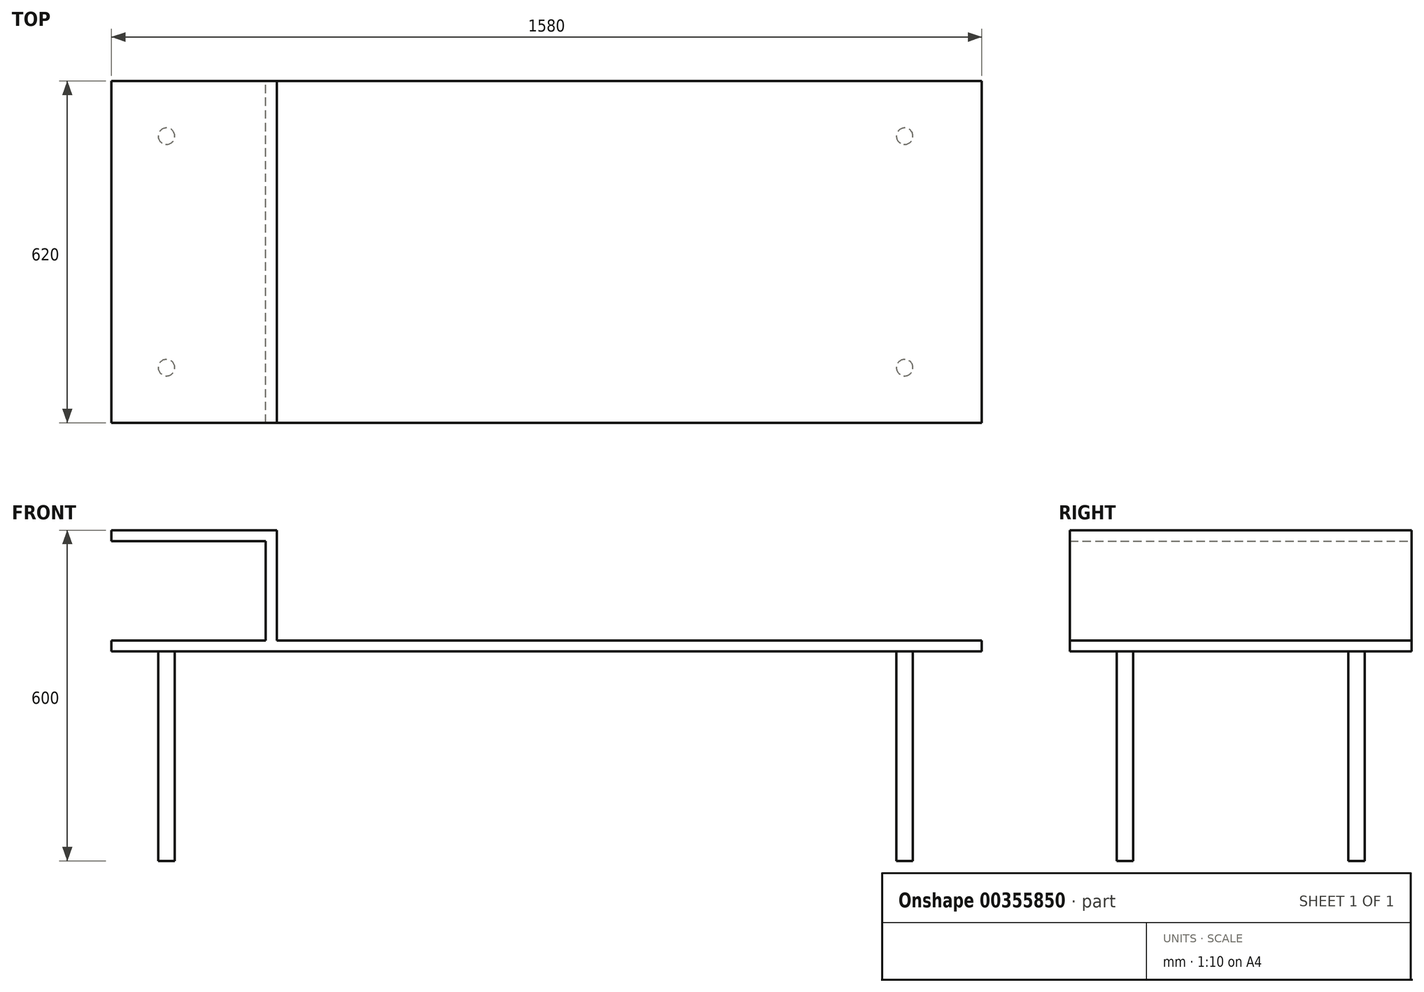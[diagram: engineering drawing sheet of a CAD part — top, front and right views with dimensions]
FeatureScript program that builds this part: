
annotation { "Feature Type Name" : "Feature", "Feature Type Description" : "" }
export const myFeature = defineFeature(function(context is Context, id is Id, definition is map)
    precondition{}
    {
        {
            var Q0;
            Q0=qCreatedBy(makeId("Front.planeOp"),FACE);
            var sketch = newSketch(context, id + "F0", { "sketchPlane" : qUnion([Q0])});
            skLineSegment(sketch, "E0.bottom", {"start": v(-20.5, 31.87) * mm, "end": v(1259.5, 31.87) * mm});
            skLineSegment(sketch, "E0.top", {"start": v(-20.5, 11.87) * mm, "end": v(1259.5, 11.87) * mm});
            skLineSegment(sketch, "E0.left", {"start": v(-20.5, 31.87) * mm, "end": v(-20.5, 11.87) * mm});
            skLineSegment(sketch, "E0.right", {"start": v(1259.5, 31.87) * mm, "end": v(1259.5, 11.87) * mm});
            skLineSegment(sketch, "E1.bottom", {"start": v(-20.5, 31.87) * mm, "end": v(-320.5, 31.87) * mm});
            skLineSegment(sketch, "E1.top", {"start": v(-20.5, 11.87) * mm, "end": v(-320.5, 11.87) * mm});
            skLineSegment(sketch, "E1.right", {"start": v(-320.5, 31.87) * mm, "end": v(-320.5, 11.87) * mm});
            skLineSegment(sketch, "E2.bottom", {"start": v(-20.5, 31.87) * mm, "end": v(-40.5, 31.87) * mm});
            skLineSegment(sketch, "E2.top", {"start": v(-20.5, 231.87) * mm, "end": v(-40.5, 231.87) * mm});
            skLineSegment(sketch, "E2.left", {"start": v(-20.5, 31.87) * mm, "end": v(-20.5, 231.87) * mm});
            skLineSegment(sketch, "E2.right", {"start": v(-40.5, 31.87) * mm, "end": v(-40.5, 231.87) * mm});
            skLineSegment(sketch, "E3.bottom", {"start": v(-20.5, 231.87) * mm, "end": v(-320.5, 231.87) * mm});
            skLineSegment(sketch, "E3.top", {"start": v(-20.5, 211.87) * mm, "end": v(-320.5, 211.87) * mm});
            skLineSegment(sketch, "E3.left", {"start": v(-20.5, 231.87) * mm, "end": v(-20.5, 211.87) * mm});
            skLineSegment(sketch, "E3.right", {"start": v(-320.5, 231.87) * mm, "end": v(-320.5, 211.87) * mm});
            skSolve(sketch);
        }
        {
            var Q0;
            Q0 = qSketchRegion(id + "F0", true);
            extrude(context, id + "F1", {"entities" : qUnion([Q0]), "depth" : 620 * mm});
        }
        {
            var Q0;
            Q0=makeQuery(id+"F1.opExtrude","SWEPT_FACE",FACE,{"disambiguationData":[OSD([sQuery(id+"F0.wireOp",EDGE,"E0.top"),sQuery(id+"F0.wireOp",EDGE,"E1.top")])]});
            var sketch = newSketch(context, id + "F2", { "sketchPlane" : qUnion([Q0])});
            skCircle(sketch, "E4", {"center": v(-220.5, 520) * mm, "radius": 15 * mm});
            skCircle(sketch, "E5", {"center": v(-220.5, 100) * mm, "radius": 15 * mm});
            skCircle(sketch, "E6", {"center": v(1119.5, 100) * mm, "radius": 15 * mm});
            skCircle(sketch, "E7", {"center": v(1119.5, 520) * mm, "radius": 15 * mm});
            skPoint(sketch, "E8.0.start.orphan", {"position": v(-320.5, 620) * mm});
            skPoint(sketch, "E9.0.start.orphan", {"position": v(-320.5, 0) * mm});
            skPoint(sketch, "E10.0.end.orphan", {"position": v(1259.5, 0) * mm});
            skPoint(sketch, "E10.0.start.orphan", {"position": v(1259.5, 620) * mm});
            skSolve(sketch);
        }
        {
            var Q0;
            Q0 = qSketchRegion(id + "F2", true);
            extrude(context, id + "F3", {"entities" : qUnion([Q0]), "operationType" : NewBodyOperationType.ADD, "depth" : 380 * mm});
        }
    });
